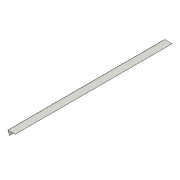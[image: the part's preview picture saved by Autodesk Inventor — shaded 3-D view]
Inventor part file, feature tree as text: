
AUTODESK INVENTOR PART (.ipt)
format: ipt  version: 2018 (Build 220112000, 112)  size: 92,160 bytes
history: native  units: in
note: dims shown in document units (in); Inventor stores cm internally (conversion verified against a paired STEP export)
features: extrude x2, sketch x2
ambient origin geometry x8: Origin, YZ Plane, XZ Plane, XY Plane, X Axis, Y Axis, Z Axis, Center Point
bodies: Solid1 (feature_tree)
feature tree (4):
  extrude  "Extrusion1"  Depth=3.0in
  extrude  "Extrusion2"  Depth=0.0747in
  sketch  "Sketch1"  dims[d0=4.0in d1=3.0in]
  sketch  "Sketch2"  dims[d2=0.0747in d3=0.0747in d4=85.0in d5=0.0in d6=15.0deg d7=1.0in d8=0.0in]
